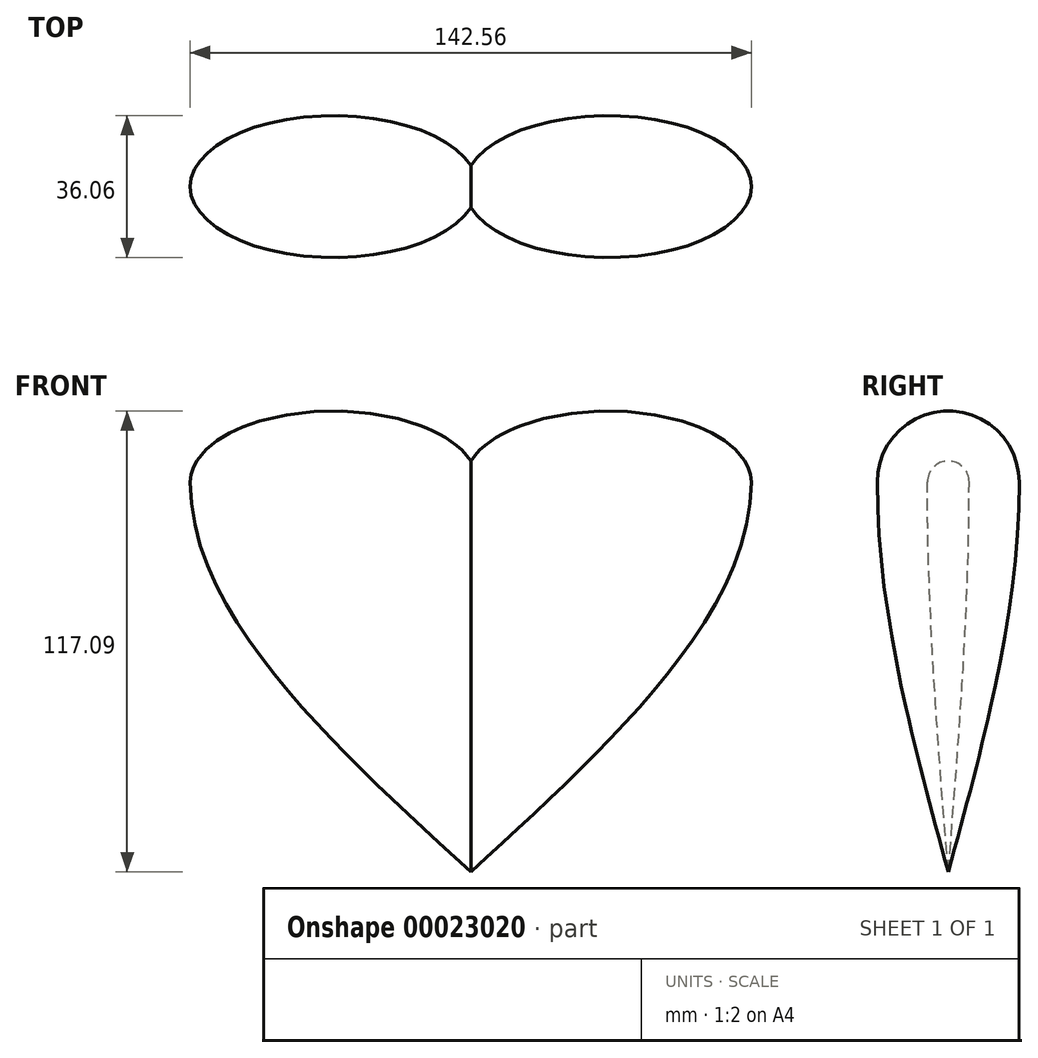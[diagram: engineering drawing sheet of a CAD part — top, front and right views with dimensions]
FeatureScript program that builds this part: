
annotation { "Feature Type Name" : "Feature", "Feature Type Description" : "" }
export const myFeature = defineFeature(function(context is Context, id is Id, definition is map)
    precondition{}
    {
        {
            var Q0;
            Q0=qCreatedBy(makeId("Top.planeOp"),FACE);
            cPlane(context, id + "F0", {"entities" : qUnion([Q0]), "cplaneType" : CPlaneType.OFFSET, "offset" : 25.4 * mm, "width" : 152.4 * mm, "height" : 152.4 * mm});
        }
        {
            var Q0;
            Q0=qCreatedBy(makeId("Top.planeOp"),FACE);
            cPlane(context, id + "F1", {"entities" : qUnion([Q0]), "cplaneType" : CPlaneType.OFFSET, "offset" : 73.66 * mm, "oppositeDirection" : true, "width" : 152.4 * mm, "height" : 152.4 * mm});
        }
        {
            var Q0;
            Q0=qCreatedBy(id+"F1.planeOp",FACE);
            var sketch = newSketch(context, id + "F2", { "sketchPlane" : qUnion([Q0])});
            skPoint(sketch, "E0.0", {"position": v(0, 0) * mm});
            skSolve(sketch);
        }
        {
            var Q0;
            Q0=qCreatedBy(id+"F0.planeOp",FACE);
            var sketch = newSketch(context, id + "F3", { "sketchPlane" : qUnion([Q0])});
            skEllipticalArc(sketch, "E1", {});
            skLineSegment(sketch, "E2", {"start": v(0, -29.75) * mm, "end": v(0, 23.4) * mm, "construction": true});
            skEllipticalArc(sketch, "E3.MirrorC", {});
            skLineSegment(sketch, "E4", {"start": v(-71.28, 0) * mm, "end": v(71.28, 0) * mm, "construction": true});
            const initialGuessF3  = {"E1": [-0.03482818976044655, 0, 1, 0, 0.03644796079816323, 0.018032196211729305, 0.29924494476937635, 5.98394036241021], "E3.MirrorC": [0.03482818976044655, 0, -1, 0, 0.03644796079816323, 0.018032196211729308, 0.29924494476937635, 5.98394036241021]};
            skSetInitialGuess(sketch, initialGuessF3);
            skSolve(sketch);
        }
        {
            var Q0;
            Q0=makeQuery(id+"F3.imprint","IMPRINT",FACE,{"disambiguationData":[TD([[makeQuery(id+"F3.imprint","IMPRINT",EDGE,{"derivedFrom":sQuery(id+"F3.wireOp",EDGE,"E1")}),1.0]])]});
            var sketch = newSketch(context, id + "F4", { "sketchPlane" : qUnion([Q0])});
            skEllipticalArc(sketch, "E5.0", {});
            skEllipticalArc(sketch, "E6.1", {});
            skLineSegment(sketch, "E7.2", {"start": v(-71.28, 0) * mm, "end": v(71.28, 0) * mm});
            const initialGuessF4  = {"E5.0": [-0.03482818976044655, 0, 1, 0, 0.03644796079816323, 0.018032196211729305, 0.29924494476937635, 5.98394036241021], "E5.0": [-0.03482818976044655, 0, 1, 0, 0.03644796079816323, 0.018032196211729305, 0.29924494476937635, 5.98394036241021], "E6.1": [0.03482818976044655, 0, -1, 0, 0.03644796079816323, 0.018032196211729308, 0.29924494476937635, 5.98394036241021], "E5.0": [-0.03482818976044655, 0, 1, 0, 0.03644796079816323, 0.018032196211729305, 0.29924494476937635, 5.98394036241021], "E6.1": [0.03482818976044655, 0, -1, 0, 0.03644796079816323, 0.018032196211729308, 0.29924494476937635, 5.98394036241021]};
            skSetInitialGuess(sketch, initialGuessF4);
            skSolve(sketch);
        }
        {
            var Q0;
            {var subQ0=sQuery(id+"F4.wireOp",EDGE,"E7.2");Q0=makeQuery(id+"F4.imprint","IMPRINT",FACE,{"disambiguationData":[TD([[makeQuery(id+"F4.imprint","IMPRINT",EDGE,{"derivedFrom":subQ0}),-1.0]])]});}
            var Q1;
            Q1=sQuery(id+"F4.wireOp",EDGE,"E7.2");
            revolve(context, id + "F5", {"entities" : qUnion([Q0]), "axis" : qUnion([Q1]), "revolveType" : RevolveType.ONE_DIRECTION, "oppositeDirection" : true, "angle" : 180 * degree});
        }
        {
            var Q1;
            Q1=sQuery(id+"F2.wireOp",VERTEX,"E0.0");
            var Q2;
            Q2=makeQuery(id+"F3.imprint","IMPRINT",FACE,{"disambiguationData":[TD([[makeQuery(id+"F3.imprint","IMPRINT",EDGE,{"derivedFrom":sQuery(id+"F3.wireOp",EDGE,"E1")}),1.0]])]});
            loft(context, id + "F6", {"operationType" : NewBodyOperationType.ADD, "endCondition" : LoftEndDerivativeType.NORMAL_TO_PROFILE, "endMagnitude" : 1, "sheetProfilesArray" : [{ "sheetProfileEntities" : qUnion([Q1]) }, { "sheetProfileEntities" : qUnion([Q2]) }]});
        }
    });
